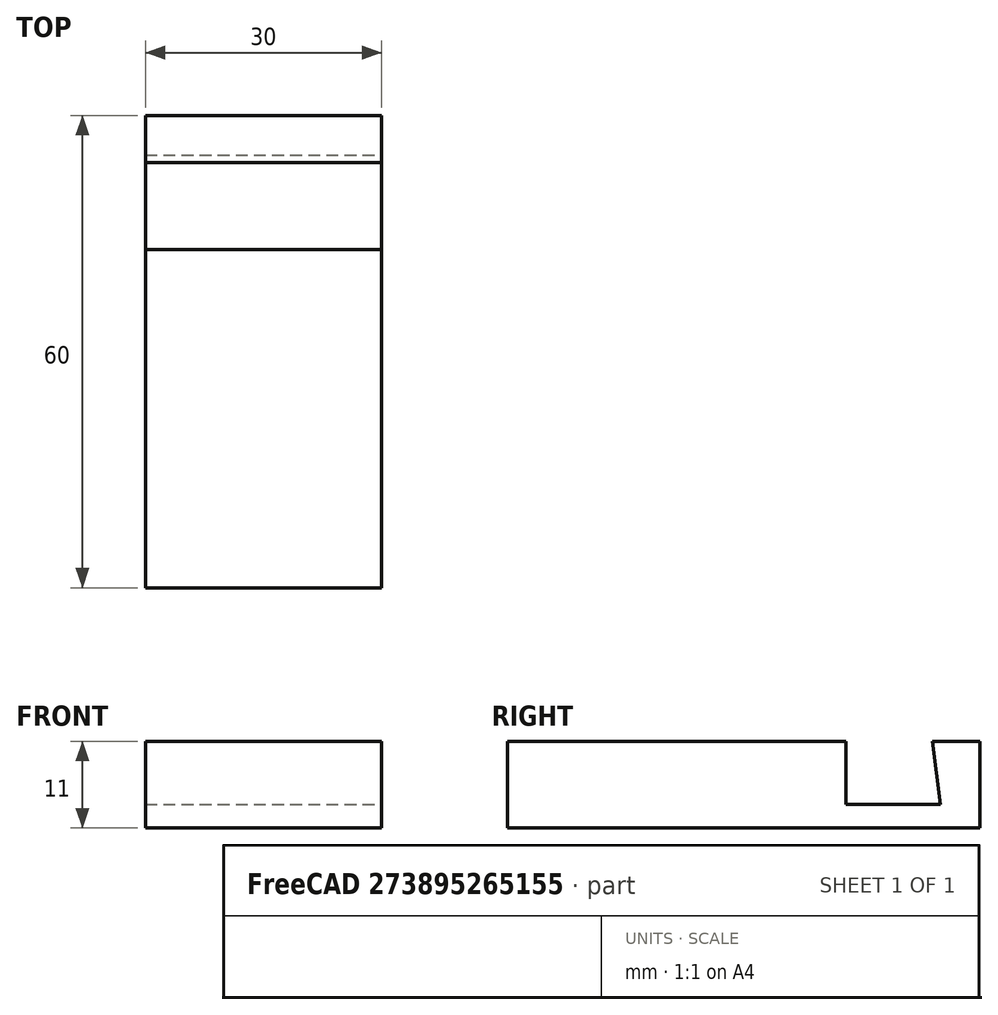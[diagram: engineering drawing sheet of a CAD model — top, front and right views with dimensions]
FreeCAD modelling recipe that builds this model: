
FCSTD DOCUMENT  (FreeCAD 0.20R29177 +233 (Git))
Label: soporte_movil
License: All rights reserved
LicenseURL: http://en.wikipedia.org/wiki/All_rights_reserved
objects: PartDesign::Body×2, Sketcher::SketchObject×1, PartDesign::Pad×1
note: 5 computed .brp shape members not serialized (recipe doc carries the construction recipe); baked Part::Feature solids carry a one-line shape summary decoded from their .brp

FEATURE [PartDesign::Body] Body
  Origin = -> Origin
FEATURE [Sketcher::SketchObject] Sketch
  FullyConstrained = true
  MapMode = 5
  Placement = pos=(0,0,0) rot=(0.57735,0.57735,0.57735;2.0944rad)
  Support = -> [YZ_Plane001]
  sketch-geometry (8):
    g0: LineSegment StartX=0 StartY=0 StartZ=0 EndX=60 EndY=0 EndZ=0
    g1: LineSegment StartX=0 StartY=0 StartZ=0 EndX=0 EndY=11 EndZ=0
    g2: LineSegment StartX=0 StartY=11 StartZ=0 EndX=43 EndY=11 EndZ=0
    g3: LineSegment StartX=43 StartY=11 StartZ=0 EndX=43 EndY=3 EndZ=0
    g4: LineSegment StartX=43 StartY=3 StartZ=0 EndX=55 EndY=3 EndZ=0
    g5: LineSegment StartX=55 StartY=3 StartZ=0 EndX=54 EndY=11 EndZ=0
    g6: LineSegment StartX=54 StartY=11 StartZ=0 EndX=60 EndY=11 EndZ=0
    g7: LineSegment StartX=60 StartY=11 StartZ=0 EndX=60 EndY=0 EndZ=0
  constraints (23):
    c: Coincident(g0,g-1)
    c: PointOnObject(g0,g-1)
    c: Distance(g0) = 60
    c: Coincident(g1,g0)
    c: PointOnObject(g1,g-2)
    c: Coincident(g2,g1)
    c: Coincident(g3,g2)
    c: Vertical(g3)
    c: Distance(g1) = 11
    c: Horizontal(g2)
    c: Coincident(g4,g3)
    c: Horizontal(g4)
    c: Distance(g4) = 12
    c: Coincident(g5,g4)
    c: Distance(g2,g5) = 11
    c: Coincident(g6,g5)
    c: Horizontal(g6)
    c: Coincident(g7,g6)
    c: Coincident(g7,g0)
    c: Distance(g6,g5) = 6
    c: Distance(g4,g0) = 3
    c: Vertical(g7)
    c: Equal(g7,g1)
FEATURE [PartDesign::Pad] Pad
  Direction = (1,-2e-16,3e-16)
  Length = 30
  Length2 = 10
  Placement = pos=(0,0,0) rot=(0.57735,0.57735,0.57735;2.0944rad)
  Profile = -> Sketch
  ReferenceAxis = -> Sketch [N_Axis]
  Type = 0
FEATURE [PartDesign::Body] Body001
  Group = -> [Sketch,Pad]
  Origin = -> Origin001
  Tip = -> Pad
